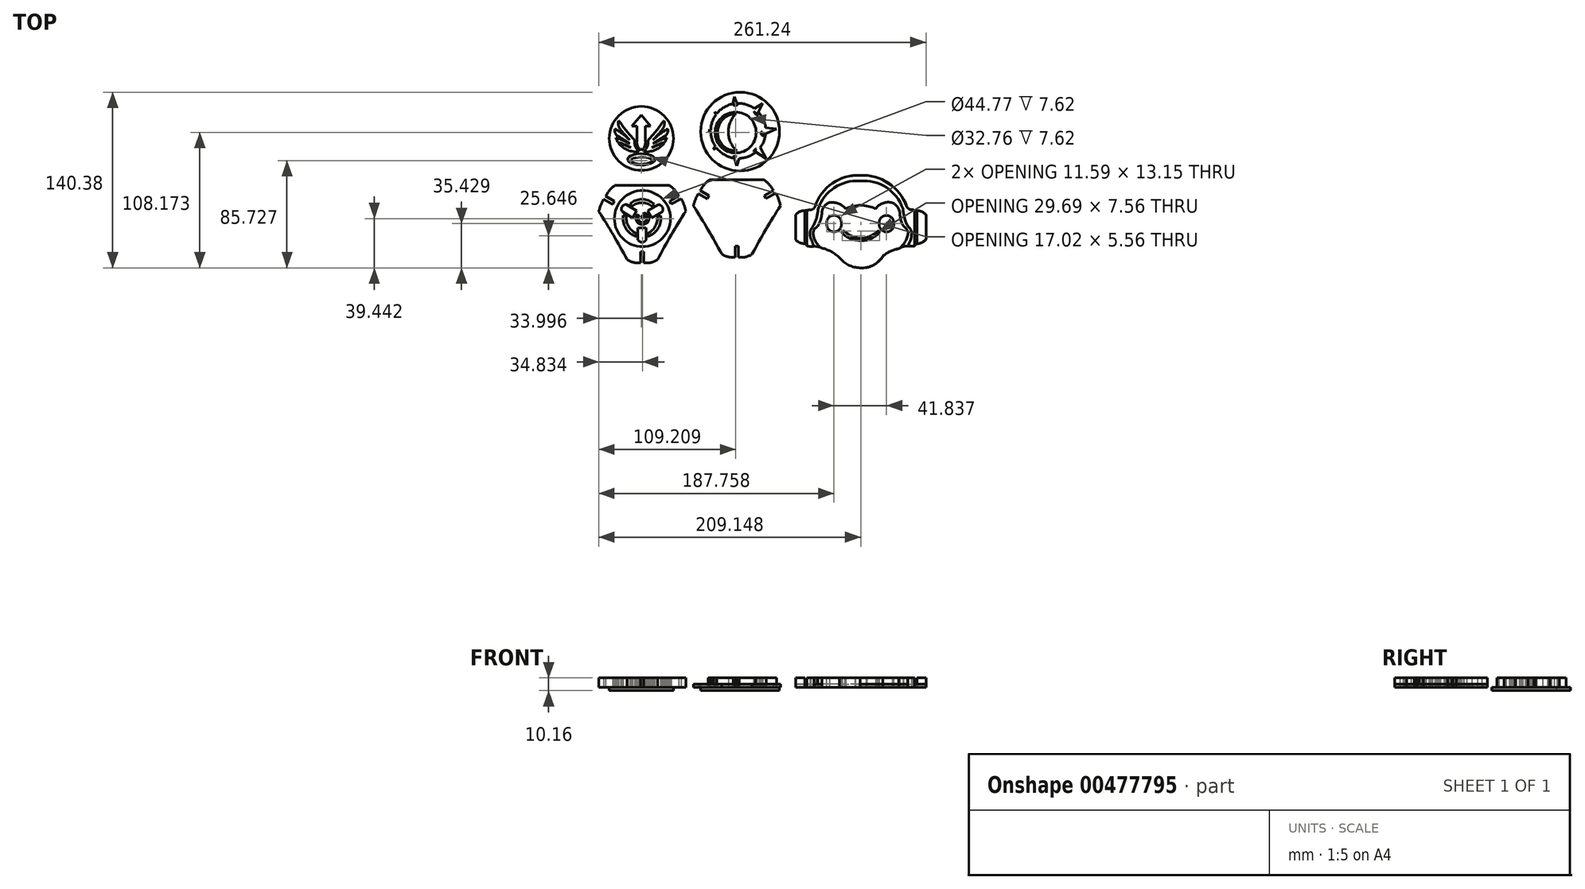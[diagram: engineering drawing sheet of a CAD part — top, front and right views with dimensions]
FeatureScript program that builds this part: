
annotation { "Feature Type Name" : "Feature", "Feature Type Description" : "" }
export const myFeature = defineFeature(function(context is Context, id is Id, definition is map)
    precondition{}
    {
        {
            var Q0;
            Q0=qCreatedBy(makeId("Top.planeOp"),FACE);
            var sketch = newSketch(context, id + "F0", { "sketchPlane" : qUnion([Q0])});
            skEllipse(sketch, "E0", {"center": v(-39.47, 12.8) * mm, "majorRadius": 10.93 * mm, "minorRadius": 4.55 * mm, "majorAxis": v(1, 0)});
            skArc(sketch, "E1", {"start": v(-39.47, 19.86) * mm, "mid": v(-36.84, 23.18) * mm, "end": v(-36.13, 27.35) * mm});
            skArc(sketch, "E2", {"start": v(-43.11, 27.35) * mm, "mid": v(-42.33, 23.1) * mm, "end": v(-39.47, 19.86) * mm});
            skLineSegment(sketch, "E3", {"start": v(-43.11, 27.35) * mm, "end": v(-43.11, 39.24) * mm});
            skLineSegment(sketch, "E4", {"start": v(-43.11, 39.24) * mm, "end": v(-46.93, 39.24) * mm});
            skLineSegment(sketch, "E5", {"start": v(-46.93, 39.24) * mm, "end": v(-39.47, 48.4) * mm});
            skLineSegment(sketch, "E6", {"start": v(-32.01, 39.24) * mm, "end": v(-36.13, 39.24) * mm});
            skLineSegment(sketch, "E7", {"start": v(-36.13, 39.24) * mm, "end": v(-36.13, 27.35) * mm});
            skLineSegment(sketch, "E8", {"start": v(-39.47, 48.4) * mm, "end": v(-32.01, 39.24) * mm});
            skArc(sketch, "E9", {"start": v(-37.54, 18.8) * mm, "mid": v(-34.69, 23.18) * mm, "end": v(-34.02, 28.37) * mm});
            skArc(sketch, "E10", {"start": v(-34.02, 28.37) * mm, "mid": v(-27.34, 35.86) * mm, "end": v(-21.41, 43.96) * mm});
            skArc(sketch, "E11", {"start": v(-22.85, 36.5) * mm, "mid": v(-21.16, 40.04) * mm, "end": v(-21.41, 43.96) * mm});
            skArc(sketch, "E12", {"start": v(-30.14, 28.37) * mm, "mid": v(-26.4, 32.35) * mm, "end": v(-22.85, 36.5) * mm});
            skArc(sketch, "E13", {"start": v(-18.2, 37.18) * mm, "mid": v(-24.47, 33.19) * mm, "end": v(-30.14, 28.37) * mm});
            skArc(sketch, "E14", {"start": v(-20.06, 31.85) * mm, "mid": v(-18.46, 34.28) * mm, "end": v(-18.2, 37.18) * mm});
            skArc(sketch, "E15", {"start": v(-20.06, 31.85) * mm, "mid": v(-25.18, 28.7) * mm, "end": v(-30.14, 25.33) * mm});
            skArc(sketch, "E16", {"start": v(-19.04, 29.98) * mm, "mid": v(-24.75, 28.03) * mm, "end": v(-30.14, 25.33) * mm});
            skArc(sketch, "E17", {"start": v(-20.84, 26.31) * mm, "mid": v(-19.86, 28.1) * mm, "end": v(-19.04, 29.98) * mm});
            skArc(sketch, "E18", {"start": v(-20.84, 26.31) * mm, "mid": v(-26.11, 24.59) * mm, "end": v(-31.06, 22.08) * mm});
            skArc(sketch, "E19", {"start": v(-21.41, 25.33) * mm, "mid": v(-26.37, 24.08) * mm, "end": v(-31.06, 22.08) * mm});
            skArc(sketch, "E20", {"start": v(-37.54, 18.8) * mm, "mid": v(-28.73, 20.22) * mm, "end": v(-21.41, 25.33) * mm});
            skLineSegment(sketch, "E21", {"start": v(-39.47, 59.1) * mm, "end": v(-39.47, -8.7) * mm, "construction": true});
            skArc(sketch, "E22.MirrorCS", {"start": v(-44.92, 28.37) * mm, "mid": v(-51.6, 35.86) * mm, "end": v(-57.52, 43.96) * mm});
            skArc(sketch, "E23.MirrorCS", {"start": v(-56.08, 36.5) * mm, "mid": v(-57.78, 40.04) * mm, "end": v(-57.52, 43.96) * mm});
            skArc(sketch, "E24.MirrorCS", {"start": v(-48.8, 28.37) * mm, "mid": v(-52.54, 32.35) * mm, "end": v(-56.08, 36.5) * mm});
            skArc(sketch, "E25.MirrorCS", {"start": v(-60.74, 37.18) * mm, "mid": v(-54.46, 33.19) * mm, "end": v(-48.8, 28.37) * mm});
            skArc(sketch, "E26.MirrorCS", {"start": v(-58.88, 31.85) * mm, "mid": v(-60.48, 34.28) * mm, "end": v(-60.74, 37.18) * mm});
            skArc(sketch, "E27.MirrorCS", {"start": v(-58.88, 31.85) * mm, "mid": v(-53.76, 28.7) * mm, "end": v(-48.8, 25.33) * mm});
            skArc(sketch, "E28.MirrorCS", {"start": v(-59.9, 29.98) * mm, "mid": v(-54.19, 28.03) * mm, "end": v(-48.8, 25.33) * mm});
            skArc(sketch, "E29.MirrorCS", {"start": v(-58.1, 26.31) * mm, "mid": v(-59.07, 28.1) * mm, "end": v(-59.9, 29.98) * mm});
            skArc(sketch, "E30.MirrorCS", {"start": v(-58.1, 26.31) * mm, "mid": v(-52.82, 24.59) * mm, "end": v(-47.87, 22.08) * mm});
            skArc(sketch, "E31.MirrorCS", {"start": v(-57.52, 25.33) * mm, "mid": v(-52.57, 24.08) * mm, "end": v(-47.87, 22.08) * mm});
            skArc(sketch, "E32.MirrorCS", {"start": v(-41.4, 18.8) * mm, "mid": v(-50.2, 20.22) * mm, "end": v(-57.52, 25.33) * mm});
            skArc(sketch, "E33.MirrorCS", {"start": v(-41.4, 18.8) * mm, "mid": v(-44.25, 23.18) * mm, "end": v(-44.92, 28.37) * mm});
            skSolve(sketch);
        }
        {
            var Q0;
            Q0 = qSketchRegion(id + "F0", true);
            extrude(context, id + "F1", {"entities" : qUnion([Q0]), "depth" : 7.62 * mm, "offsetDistance" : 25.4 * mm});
        }
        {
            var Q0;
            Q0=makeQuery(id+"F1.opExtrude","CAP_FACE",FACE,{"disambiguationData":[OSD([sQuery(id+"F0.wireOp",EDGE,"E0")])],"isStart":false});
            var sketch = newSketch(context, id + "F2", { "sketchPlane" : qUnion([Q0])});
            skEllipse(sketch, "E34", {"center": v(-39.42, 11.8) * mm, "majorRadius": 8.5 * mm, "minorRadius": 2.78 * mm, "majorAxis": v(1, 0)});
            skSolve(sketch);
        }
        {
            var Q0;
            Q0 = qSketchRegion(id + "F2", true);
            extrude(context, id + "F3", {"entities" : qUnion([Q0]), "operationType" : NewBodyOperationType.REMOVE, "oppositeDirection" : true, "depth" : 10.16 * mm, "offsetDistance" : 25.4 * mm});
        }
        {
            var Q0;
            Q0=qCreatedBy(makeId("Top.planeOp"),FACE);
            var sketch = newSketch(context, id + "F4", { "sketchPlane" : qUnion([Q0])});
            skCircle(sketch, "E35", {"center": v(37.9, 35.55) * mm, "radius": 22 * mm});
            skLineSegment(sketch, "E36", {"start": v(33.1, 54.95) * mm, "end": v(34.78, 62.86) * mm});
            skLineSegment(sketch, "E37", {"start": v(34.78, 62.86) * mm, "end": v(37.66, 54.71) * mm});
            skLineSegment(sketch, "E38", {"start": v(37.66, 54.71) * mm, "end": v(33.1, 54.95) * mm});
            skLineSegment(sketch, "E39", {"start": v(47.96, 51.6) * mm, "end": v(57.46, 57.33) * mm});
            skLineSegment(sketch, "E40", {"start": v(57.46, 57.33) * mm, "end": v(52.27, 47.29) * mm});
            skLineSegment(sketch, "E41", {"start": v(52.27, 47.29) * mm, "end": v(47.96, 51.6) * mm});
            skLineSegment(sketch, "E42", {"start": v(56.58, 38.7) * mm, "end": v(68.54, 37) * mm});
            skLineSegment(sketch, "E43", {"start": v(68.54, 37) * mm, "end": v(54.44, 31.15) * mm});
            skLineSegment(sketch, "E44", {"start": v(54.44, 31.15) * mm, "end": v(56.58, 38.7) * mm});
            skLineSegment(sketch, "E45", {"start": v(52.3, 28.3) * mm, "end": v(60.12, 13.3) * mm});
            skLineSegment(sketch, "E46", {"start": v(60.12, 13.3) * mm, "end": v(46.46, 22.46) * mm});
            skLineSegment(sketch, "E47", {"start": v(46.46, 22.46) * mm, "end": v(52.3, 28.3) * mm});
            skLineSegment(sketch, "E48", {"start": v(40.3, 18.87) * mm, "end": v(36.67, 7.48) * mm});
            skLineSegment(sketch, "E49", {"start": v(36.67, 7.48) * mm, "end": v(32.79, 19.35) * mm});
            skLineSegment(sketch, "E50", {"start": v(32.79, 19.35) * mm, "end": v(40.3, 18.87) * mm});
            skLineSegment(sketch, "E51", {"start": v(21.25, 25.6) * mm, "end": v(23.53, 23.32) * mm});
            skLineSegment(sketch, "E52", {"start": v(19.4, 37) * mm, "end": v(18.83, 34) * mm});
            skLineSegment(sketch, "E53", {"start": v(21.25, 46.25) * mm, "end": v(18.83, 50.9) * mm});
            skLineSegment(sketch, "E54", {"start": v(18.83, 50.9) * mm, "end": v(23.53, 47.82) * mm});
            skLineSegment(sketch, "E55", {"start": v(23.53, 47.82) * mm, "end": v(21.25, 46.25) * mm});
            skLineSegment(sketch, "E56", {"start": v(21.25, 25.6) * mm, "end": v(18, 20.57) * mm});
            skLineSegment(sketch, "E57", {"start": v(18, 20.57) * mm, "end": v(23.53, 23.32) * mm});
            skLineSegment(sketch, "E58", {"start": v(18.83, 34) * mm, "end": v(13.83, 35.9) * mm});
            skLineSegment(sketch, "E59", {"start": v(13.83, 35.9) * mm, "end": v(19.4, 37) * mm});
            skSolve(sketch);
        }
        {
            var Q0;
            Q0 = qSketchRegion(id + "F4", true);
            extrude(context, id + "F5", {"entities" : qUnion([Q0]), "depth" : 7.62 * mm, "offsetDistance" : 25.4 * mm});
        }
        {
            var Q0;
            Q0=makeQuery(id+"F5.opExtrude","CAP_FACE",FACE,{"disambiguationData":[OSD([sQuery(id+"F4.wireOp",EDGE,"E35"),sQuery(id+"F4.wireOp",EDGE,"E36"),sQuery(id+"F4.wireOp",EDGE,"E37"),sQuery(id+"F4.wireOp",EDGE,"E39"),sQuery(id+"F4.wireOp",EDGE,"E40"),sQuery(id+"F4.wireOp",EDGE,"E42"),sQuery(id+"F4.wireOp",EDGE,"E43"),sQuery(id+"F4.wireOp",EDGE,"E45"),sQuery(id+"F4.wireOp",EDGE,"E46"),sQuery(id+"F4.wireOp",EDGE,"E48"),sQuery(id+"F4.wireOp",EDGE,"E49"),sQuery(id+"F4.wireOp",EDGE,"lFvAN2aY-k7Z1-D6F1-dTq4-gRtL9pACbP7c"),sQuery(id+"F4.wireOp",EDGE,"jxr9UWhJ-qfHT-bBvY-aeZa-IXjNacF00unG"),sQuery(id+"F4.wireOp",EDGE,"2JyZSbPP-UnY0-dJu7-hiOL-rgGKe5CIZ8wm"),sQuery(id+"F4.wireOp",EDGE,"D89O3qcm-xly6-wlmF-0ntx-pCZKfBFehd9C"),sQuery(id+"F4.wireOp",EDGE,"E53"),sQuery(id+"F4.wireOp",EDGE,"E54")])],"isStart":false});
            var sketch = newSketch(context, id + "F6", { "sketchPlane" : qUnion([Q0])});
            skCircle(sketch, "E60", {"center": v(35.79, 34.25) * mm, "radius": 16.38 * mm});
            skPoint(sketch, "E60.first.point", {"position": v(19.41, 34.57) * mm});
            skPoint(sketch, "E60.second.point", {"position": v(52.17, 34.57) * mm});
            skPoint(sketch, "E60.third.point", {"position": v(42.9, 49) * mm});
            skLineSegment(sketch, "E61", {"start": v(36.67, 57.51) * mm, "end": v(36.93, 56.85) * mm});
            skArc(sketch, "E62", {"start": v(37.26, 57.54) * mm, "mid": v(36.95, 57.93) * mm, "end": v(36.67, 57.51) * mm});
            skArc(sketch, "E63", {"start": v(34.61, 56.5) * mm, "mid": v(35.8, 56.52) * mm, "end": v(36.93, 56.85) * mm});
            skArc(sketch, "E64", {"start": v(34.61, 55.75) * mm, "mid": v(35.78, 55.84) * mm, "end": v(36.9, 56.13) * mm});
            skLineSegment(sketch, "E65", {"start": v(59.79, 33.37) * mm, "end": v(57.57, 32.45) * mm});
            skArc(sketch, "E66", {"start": v(57.06, 34.3) * mm, "mid": v(57.21, 33.34) * mm, "end": v(57.57, 32.45) * mm});
            skLineSegment(sketch, "E67", {"start": v(58.16, 31.82) * mm, "end": v(60.29, 32.7) * mm});
            skLineSegment(sketch, "E68", {"start": v(60.29, 32.7) * mm, "end": v(59.79, 33.37) * mm});
            skLineSegment(sketch, "E69", {"start": v(52.06, 18.71) * mm, "end": v(51.37, 19.17) * mm});
            skArc(sketch, "E70", {"start": v(52.44, 21.37) * mm, "mid": v(51.66, 20.39) * mm, "end": v(51.37, 19.17) * mm});
            skArc(sketch, "E71", {"start": v(52.44, 21.37) * mm, "mid": v(51.12, 20.55) * mm, "end": v(50.39, 19.17) * mm});
            skLineSegment(sketch, "E72", {"start": v(50.39, 19.17) * mm, "end": v(51.93, 18.14) * mm});
            skLineSegment(sketch, "E73", {"start": v(51.93, 18.14) * mm, "end": v(52.06, 18.71) * mm});
            skLineSegment(sketch, "E74", {"start": v(53.97, 50.57) * mm, "end": v(53.28, 49.24) * mm});
            skLineSegment(sketch, "E75", {"start": v(53.86, 48.6) * mm, "end": v(55.03, 50.86) * mm});
            skLineSegment(sketch, "E76", {"start": v(55.03, 50.86) * mm, "end": v(53.97, 50.57) * mm});
            skArc(sketch, "E77", {"start": v(50.65, 51.26) * mm, "mid": v(51.75, 49.97) * mm, "end": v(53.28, 49.24) * mm});
            skArc(sketch, "E78", {"start": v(50.65, 51.26) * mm, "mid": v(51.39, 49.24) * mm, "end": v(53.3, 48.23) * mm});
            skLineSegment(sketch, "E79", {"start": v(34.6, 13.8) * mm, "end": v(34.4, 14.45) * mm});
            skArc(sketch, "E80", {"start": v(36.28, 15) * mm, "mid": v(35.3, 14.88) * mm, "end": v(34.4, 14.45) * mm});
            skArc(sketch, "E81", {"start": v(36.28, 15) * mm, "mid": v(34.94, 15.27) * mm, "end": v(33.66, 14.76) * mm});
            skLineSegment(sketch, "E82", {"start": v(33.66, 14.76) * mm, "end": v(34.12, 13.36) * mm});
            skLineSegment(sketch, "E83", {"start": v(34.12, 13.36) * mm, "end": v(34.6, 13.8) * mm});
            skArc(sketch, "E84", {"start": v(56.77, 34.99) * mm, "mid": v(56.9, 34.63) * mm, "end": v(57.06, 34.3) * mm});
            skArc(sketch, "E85", {"start": v(53.3, 48.23) * mm, "mid": v(53.62, 48.34) * mm, "end": v(53.86, 48.6) * mm});
            skArc(sketch, "E86", {"start": v(56.77, 34.99) * mm, "mid": v(56.3, 34.58) * mm, "end": v(56.13, 33.97) * mm});
            skArc(sketch, "E87", {"start": v(56.13, 33.97) * mm, "mid": v(56.36, 32.83) * mm, "end": v(56.98, 31.85) * mm});
            skArc(sketch, "E88", {"start": v(56.98, 31.85) * mm, "mid": v(57.57, 31.71) * mm, "end": v(58.16, 31.82) * mm});
            skArc(sketch, "E89", {"start": v(34.61, 56.5) * mm, "mid": v(34.33, 56.49) * mm, "end": v(34.09, 56.33) * mm});
            skArc(sketch, "E90", {"start": v(34.09, 56.33) * mm, "mid": v(34.26, 55.96) * mm, "end": v(34.61, 55.75) * mm});
            skArc(sketch, "E91", {"start": v(36.9, 56.13) * mm, "mid": v(37.52, 56.72) * mm, "end": v(37.26, 57.54) * mm});
            skSolve(sketch);
        }
        {
            var Q0;
            Q0 = qSketchRegion(id + "F6", true);
            extrude(context, id + "F7", {"entities" : qUnion([Q0]), "operationType" : NewBodyOperationType.REMOVE, "oppositeDirection" : true, "depth" : 10.16 * mm, "offsetDistance" : 25.4 * mm});
        }
        {
            var Q0;
            Q0=qCreatedBy(makeId("Top.planeOp"),FACE);
            var sketch = newSketch(context, id + "F8", { "sketchPlane" : qUnion([Q0])});
            skArc(sketch, "E92", {"start": v(35.97, 49.24) * mm, "mid": v(21.34, 33.96) * mm, "end": v(36.82, 19.55) * mm});
            skArc(sketch, "E93", {"start": v(35.97, 49.24) * mm, "mid": v(30, 34.2) * mm, "end": v(36.82, 19.55) * mm});
            skSolve(sketch);
        }
        {
            var Q0;
            Q0 = qSketchRegion(id + "F8", true);
            extrude(context, id + "F9", {"entities" : qUnion([Q0]), "depth" : 7.62 * mm, "offsetDistance" : 25.4 * mm});
        }
        {
            var Q0;
            Q0=qCreatedBy(makeId("Top.planeOp"),FACE);
            var sketch = newSketch(context, id + "F10", { "sketchPlane" : qUnion([Q0])});
            skArc(sketch, "E94", {"start": v(-50.93, -67.1) * mm, "mid": v(-61.81, -47.72) * mm, "end": v(-73.42, -28.77) * mm});
            skArc(sketch, "E95", {"start": v(-69.5, -19.18) * mm, "mid": v(-71.85, -23.81) * mm, "end": v(-73.42, -28.77) * mm});
            skLineSegment(sketch, "E96", {"start": v(-69.5, -19.18) * mm, "end": v(-62.35, -23.13) * mm});
            skLineSegment(sketch, "E97", {"start": v(-62.35, -23.13) * mm, "end": v(-61.02, -20.72) * mm});
            skLineSegment(sketch, "E98", {"start": v(-61.02, -20.72) * mm, "end": v(-67.87, -16.43) * mm});
            skArc(sketch, "E99", {"start": v(-60.6, -8.06) * mm, "mid": v(-64.75, -11.8) * mm, "end": v(-67.87, -16.43) * mm});
            skLineSegment(sketch, "E100", {"start": v(-60.6, -8.06) * mm, "end": v(-16.9, -8.06) * mm});
            skArc(sketch, "E101", {"start": v(-9.62, -16.43) * mm, "mid": v(-12.8, -11.84) * mm, "end": v(-16.9, -8.06) * mm});
            skLineSegment(sketch, "E102", {"start": v(-9.62, -16.43) * mm, "end": v(-16.88, -20.7) * mm});
            skLineSegment(sketch, "E103", {"start": v(-16.88, -20.7) * mm, "end": v(-15.53, -23) * mm});
            skLineSegment(sketch, "E104", {"start": v(-15.53, -23) * mm, "end": v(-7.67, -18.62) * mm});
            skArc(sketch, "E105", {"start": v(-3.93, -28.59) * mm, "mid": v(-5.43, -23.47) * mm, "end": v(-7.67, -18.62) * mm});
            skArc(sketch, "E106", {"start": v(-3.93, -28.59) * mm, "mid": v(-15.66, -47.74) * mm, "end": v(-26.59, -67.38) * mm});
            skArc(sketch, "E107", {"start": v(-50.93, -67.1) * mm, "mid": v(-45.82, -69.52) * mm, "end": v(-40.18, -69.82) * mm});
            skLineSegment(sketch, "E108", {"start": v(-40.18, -69.82) * mm, "end": v(-40.18, -60.92) * mm});
            skLineSegment(sketch, "E109", {"start": v(-40.18, -60.92) * mm, "end": v(-37.45, -60.92) * mm});
            skLineSegment(sketch, "E110", {"start": v(-37.45, -60.92) * mm, "end": v(-37.45, -69.82) * mm});
            skArc(sketch, "E111", {"start": v(-37.45, -69.82) * mm, "mid": v(-31.8, -69.59) * mm, "end": v(-26.59, -67.38) * mm});
            skSolve(sketch);
        }
        {
            var Q0;
            Q0 = qSketchRegion(id + "F10", true);
            extrude(context, id + "F11", {"entities" : qUnion([Q0]), "depth" : 7.62 * mm, "offsetDistance" : 25.4 * mm});
        }
        {
            var Q0;
            Q0=makeQuery(id+"F11.opExtrude","CAP_FACE",FACE,{"disambiguationData":[OSD([sQuery(id+"F10.wireOp",EDGE,"E94"),sQuery(id+"F10.wireOp",EDGE,"E95"),sQuery(id+"F10.wireOp",EDGE,"E96"),sQuery(id+"F10.wireOp",EDGE,"E97"),sQuery(id+"F10.wireOp",EDGE,"E98"),sQuery(id+"F10.wireOp",EDGE,"E99"),sQuery(id+"F10.wireOp",EDGE,"E100"),sQuery(id+"F10.wireOp",EDGE,"E101"),sQuery(id+"F10.wireOp",EDGE,"E102"),sQuery(id+"F10.wireOp",EDGE,"E103"),sQuery(id+"F10.wireOp",EDGE,"E104"),sQuery(id+"F10.wireOp",EDGE,"E105"),sQuery(id+"F10.wireOp",EDGE,"E106"),sQuery(id+"F10.wireOp",EDGE,"E107"),sQuery(id+"F10.wireOp",EDGE,"E108"),sQuery(id+"F10.wireOp",EDGE,"E109"),sQuery(id+"F10.wireOp",EDGE,"E110"),sQuery(id+"F10.wireOp",EDGE,"E111")])],"isStart":false});
            var sketch = newSketch(context, id + "F12", { "sketchPlane" : qUnion([Q0])});
            skCircle(sketch, "E112", {"center": v(-38.59, -34.48) * mm, "radius": 22.38 * mm});
            skSolve(sketch);
        }
        {
            var Q0;
            Q0 = qSketchRegion(id + "F12", true);
            extrude(context, id + "F13", {"entities" : qUnion([Q0]), "operationType" : NewBodyOperationType.REMOVE, "oppositeDirection" : true, "depth" : 25.4 * mm, "offsetDistance" : 25.4 * mm});
        }
        {
            var Q0;
            Q0=qCreatedBy(makeId("Top.planeOp"),FACE);
            var sketch = newSketch(context, id + "F14", { "sketchPlane" : qUnion([Q0])});
            skLineSegment(sketch, "E113", {"start": v(-42.22, -41.82) * mm, "end": v(-35.6, -41.82) * mm});
            skLineSegment(sketch, "E114", {"start": v(-35.6, -41.82) * mm, "end": v(-35.6, -51.3) * mm});
            skLineSegment(sketch, "E115", {"start": v(-42.22, -41.82) * mm, "end": v(-42.22, -51.3) * mm});
            skArc(sketch, "E116", {"start": v(-42.22, -51.3) * mm, "mid": v(-38.9, -53.4) * mm, "end": v(-35.6, -51.3) * mm});
            skLineSegment(sketch, "E117", {"start": v(-43.22, -28.1) * mm, "end": v(-46.56, -33.83) * mm});
            skLineSegment(sketch, "E118", {"start": v(-46.56, -33.83) * mm, "end": v(-54.74, -29.04) * mm});
            skLineSegment(sketch, "E119", {"start": v(-43.22, -28.1) * mm, "end": v(-51.4, -23.32) * mm});
            skArc(sketch, "E120", {"start": v(-51.4, -23.32) * mm, "mid": v(-54.88, -25.12) * mm, "end": v(-54.74, -29.04) * mm});
            skLineSegment(sketch, "E121.0", {"start": v(-51.4, -23.32) * mm, "end": v(-54.74, -29.04) * mm, "construction": true});
            skLineSegment(sketch, "E122", {"start": v(-31.08, -33.87) * mm, "end": v(-34.39, -28.13) * mm});
            skLineSegment(sketch, "E123", {"start": v(-34.39, -28.13) * mm, "end": v(-26.18, -23.39) * mm});
            skLineSegment(sketch, "E124", {"start": v(-31.08, -33.87) * mm, "end": v(-22.87, -29.13) * mm});
            skArc(sketch, "E125", {"start": v(-22.87, -29.13) * mm, "mid": v(-22.7, -25.21) * mm, "end": v(-26.18, -23.39) * mm});
            skLineSegment(sketch, "E126.0", {"start": v(-22.87, -29.13) * mm, "end": v(-26.18, -23.39) * mm, "construction": true});
            skArc(sketch, "E127", {"start": v(-51.55, -31.93) * mm, "mid": v(-49.83, -40.42) * mm, "end": v(-43.59, -46.41) * mm});
            skLineSegment(sketch, "E128", {"start": v(-51.55, -31.93) * mm, "end": v(-53.95, -31.93) * mm});
            skLineSegment(sketch, "E129", {"start": v(-43.59, -46.41) * mm, "end": v(-43.65, -48.86) * mm});
            skArc(sketch, "E130", {"start": v(-53.95, -31.93) * mm, "mid": v(-51.9, -42.28) * mm, "end": v(-43.65, -48.86) * mm});
            skArc(sketch, "E131.MirrorCS", {"start": v(-26.48, -31.94) * mm, "mid": v(-28.2, -40.42) * mm, "end": v(-34.45, -46.42) * mm});
            skArc(sketch, "E132.MirrorCS", {"start": v(-24.09, -31.94) * mm, "mid": v(-26.14, -42.29) * mm, "end": v(-34.39, -48.86) * mm});
            skLineSegment(sketch, "E133.MirrorCS", {"start": v(-26.48, -31.94) * mm, "end": v(-24.09, -31.94) * mm});
            skLineSegment(sketch, "E134.MirrorCS", {"start": v(-34.45, -46.42) * mm, "end": v(-34.39, -48.86) * mm});
            skLineSegment(sketch, "E135", {"start": v(-46.94, -24.7) * mm, "end": v(-48.37, -22.61) * mm});
            skLineSegment(sketch, "E136", {"start": v(-31.02, -24.7) * mm, "end": v(-29.4, -22.76) * mm});
            skArc(sketch, "E137", {"start": v(-29.4, -22.76) * mm, "mid": v(-38.85, -19.13) * mm, "end": v(-48.37, -22.61) * mm});
            skArc(sketch, "E138", {"start": v(-31.02, -24.7) * mm, "mid": v(-38.98, -21.9) * mm, "end": v(-46.94, -24.7) * mm});
            skLineSegment(sketch, "E139", {"start": v(-42.47, -31.32) * mm, "end": v(-41.2, -32.2) * mm});
            skArc(sketch, "E140", {"start": v(-41.2, -32.2) * mm, "mid": v(-41.75, -35.3) * mm, "end": v(-39.36, -37.38) * mm});
            skArc(sketch, "E141", {"start": v(-39.36, -37.38) * mm, "mid": v(-36.44, -36.71) * mm, "end": v(-35.3, -33.95) * mm});
            skArc(sketch, "E142", {"start": v(-35.3, -33.95) * mm, "mid": v(-35.66, -32.87) * mm, "end": v(-36.6, -32.2) * mm});
            skLineSegment(sketch, "E143", {"start": v(-36.6, -32.2) * mm, "end": v(-38.37, -34.65) * mm});
            skLineSegment(sketch, "E144", {"start": v(-38.37, -34.65) * mm, "end": v(-39.73, -33.66) * mm});
            skLineSegment(sketch, "E145", {"start": v(-39.73, -33.66) * mm, "end": v(-37.07, -30) * mm});
            skArc(sketch, "E146", {"start": v(-34.84, -37.9) * mm, "mid": v(-33.51, -33.26) * mm, "end": v(-37.07, -30) * mm});
            skArc(sketch, "E147", {"start": v(-42.47, -31.32) * mm, "mid": v(-43.65, -35.6) * mm, "end": v(-40.67, -38.88) * mm});
            skArc(sketch, "E148", {"start": v(-40.67, -38.88) * mm, "mid": v(-37.62, -39.2) * mm, "end": v(-34.84, -37.9) * mm});
            skSolve(sketch);
        }
        {
            var Q0;
            Q0 = qSketchRegion(id + "F14", true);
            extrude(context, id + "F15", {"entities" : qUnion([Q0]), "depth" : 7.62 * mm, "offsetDistance" : 25.4 * mm});
        }
        {
            var Q0;
            Q0=qCreatedBy(makeId("Top.planeOp"),FACE);
            var sketch = newSketch(context, id + "F16", { "sketchPlane" : qUnion([Q0])});
            skArc(sketch, "E149", {"start": v(24.6, -62.68) * mm, "mid": v(13.72, -43.3) * mm, "end": v(2.11, -24.34) * mm});
            skArc(sketch, "E150", {"start": v(6.03, -14.76) * mm, "mid": v(3.68, -19.4) * mm, "end": v(2.11, -24.34) * mm});
            skLineSegment(sketch, "E151", {"start": v(6.03, -14.76) * mm, "end": v(13.19, -18.7) * mm});
            skLineSegment(sketch, "E152", {"start": v(13.19, -18.7) * mm, "end": v(14.51, -16.3) * mm});
            skLineSegment(sketch, "E153", {"start": v(14.51, -16.3) * mm, "end": v(7.66, -12) * mm});
            skArc(sketch, "E154", {"start": v(14.94, -3.64) * mm, "mid": v(10.78, -7.37) * mm, "end": v(7.66, -12) * mm});
            skLineSegment(sketch, "E155", {"start": v(14.94, -3.64) * mm, "end": v(58.63, -3.64) * mm});
            skArc(sketch, "E156", {"start": v(65.91, -12) * mm, "mid": v(62.73, -7.42) * mm, "end": v(58.63, -3.64) * mm});
            skLineSegment(sketch, "E157", {"start": v(65.91, -12) * mm, "end": v(58.65, -16.29) * mm});
            skLineSegment(sketch, "E158", {"start": v(58.65, -16.29) * mm, "end": v(60, -18.58) * mm});
            skLineSegment(sketch, "E159", {"start": v(60, -18.58) * mm, "end": v(67.87, -14.2) * mm});
            skArc(sketch, "E160", {"start": v(71.6, -24.16) * mm, "mid": v(70.1, -19.04) * mm, "end": v(67.87, -14.2) * mm});
            skArc(sketch, "E161", {"start": v(71.6, -24.16) * mm, "mid": v(59.87, -43.32) * mm, "end": v(48.94, -62.95) * mm});
            skArc(sketch, "E162", {"start": v(24.6, -62.68) * mm, "mid": v(29.71, -65.1) * mm, "end": v(35.35, -65.4) * mm});
            skLineSegment(sketch, "E163", {"start": v(35.35, -65.4) * mm, "end": v(35.35, -56.5) * mm});
            skLineSegment(sketch, "E164", {"start": v(35.35, -56.5) * mm, "end": v(38.09, -56.5) * mm});
            skLineSegment(sketch, "E165", {"start": v(38.09, -56.5) * mm, "end": v(38.09, -65.4) * mm});
            skArc(sketch, "E166", {"start": v(38.09, -65.4) * mm, "mid": v(43.74, -65.16) * mm, "end": v(48.94, -62.95) * mm});
            skSolve(sketch);
        }
        {
            var Q0;
            Q0 = qSketchRegion(id + "F16", true);
            extrude(context, id + "F17", {"entities" : qUnion([Q0]), "depth" : 2.54 * mm, "offsetDistance" : 25.4 * mm});
        }
        {
            var Q0;
            Q0=qCreatedBy(makeId("Top.planeOp"),FACE);
            var sketch = newSketch(context, id + "F18", { "sketchPlane" : qUnion([Q0])});
            skArc(sketch, "E167", {"start": v(135.1, -73.85) * mm, "mid": v(145.56, -71.78) * mm, "end": v(153.35, -64.48) * mm});
            skArc(sketch, "E168", {"start": v(166.01, -58.55) * mm, "mid": v(159.28, -60.66) * mm, "end": v(153.35, -64.48) * mm});
            skArc(sketch, "E169", {"start": v(166.01, -58.55) * mm, "mid": v(171.09, -53) * mm, "end": v(173.58, -45.9) * mm});
            skArc(sketch, "E170", {"start": v(173.58, -45.9) * mm, "mid": v(172.2, -42.79) * mm, "end": v(169.82, -40.38) * mm});
            skArc(sketch, "E171", {"start": v(167.05, -31.44) * mm, "mid": v(167.77, -36.12) * mm, "end": v(169.82, -40.38) * mm});
            skArc(sketch, "E172", {"start": v(167.05, -31.44) * mm, "mid": v(165.37, -25.8) * mm, "end": v(161.03, -21.83) * mm});
            skArc(sketch, "E173", {"start": v(161.03, -21.83) * mm, "mid": v(153.52, -22.16) * mm, "end": v(147.55, -26.74) * mm});
            skArc(sketch, "E174", {"start": v(147.55, -26.74) * mm, "mid": v(135.64, -23.92) * mm, "end": v(123.73, -26.74) * mm});
            skArc(sketch, "E175", {"start": v(123.73, -26.74) * mm, "mid": v(117.89, -22.59) * mm, "end": v(110.78, -21.6) * mm});
            skArc(sketch, "E176", {"start": v(110.78, -21.6) * mm, "mid": v(106.15, -25.28) * mm, "end": v(104.62, -31) * mm});
            skArc(sketch, "E177", {"start": v(101.2, -40.87) * mm, "mid": v(103.37, -36.1) * mm, "end": v(104.62, -31) * mm});
            skArc(sketch, "E178", {"start": v(101.2, -40.87) * mm, "mid": v(99.22, -42.45) * mm, "end": v(97.87, -44.59) * mm});
            skArc(sketch, "E179", {"start": v(97.87, -44.59) * mm, "mid": v(98.4, -50.18) * mm, "end": v(101.2, -55.05) * mm});
            skArc(sketch, "E180", {"start": v(101.2, -55.05) * mm, "mid": v(102.77, -56.7) * mm, "end": v(104.62, -58.02) * mm});
            skArc(sketch, "E181", {"start": v(118.77, -65.67) * mm, "mid": v(112.2, -60.93) * mm, "end": v(104.62, -58.02) * mm});
            skArc(sketch, "E182", {"start": v(118.77, -65.67) * mm, "mid": v(126, -71.62) * mm, "end": v(135.1, -73.85) * mm});
            skArc(sketch, "E183", {"start": v(95.62, -49.66) * mm, "mid": v(96.95, -53.19) * mm, "end": v(98.46, -56.64) * mm});
            skArc(sketch, "E184", {"start": v(95.62, -43.85) * mm, "mid": v(95.13, -46.76) * mm, "end": v(95.62, -49.66) * mm});
            skArc(sketch, "E185", {"start": v(98.43, -39.3) * mm, "mid": v(96.97, -41.54) * mm, "end": v(95.62, -43.85) * mm});
            skArc(sketch, "E186", {"start": v(98.43, -39.3) * mm, "mid": v(100.65, -33.03) * mm, "end": v(101.74, -26.46) * mm});
            skArc(sketch, "E187", {"start": v(135.1, -4.55) * mm, "mid": v(114.66, -9.78) * mm, "end": v(101.74, -26.46) * mm});
            skArc(sketch, "E188", {"start": v(169.34, -26.74) * mm, "mid": v(156.1, -9.66) * mm, "end": v(135.1, -4.55) * mm});
            skArc(sketch, "E189", {"start": v(169.34, -26.74) * mm, "mid": v(170.64, -33.87) * mm, "end": v(173.19, -40.67) * mm});
            skArc(sketch, "E190", {"start": v(176.27, -44.9) * mm, "mid": v(175.03, -42.56) * mm, "end": v(173.19, -40.67) * mm});
            skArc(sketch, "E191", {"start": v(173.19, -56.4) * mm, "mid": v(175.67, -50.9) * mm, "end": v(176.27, -44.9) * mm});
            skArc(sketch, "E192", {"start": v(173.19, -56.4) * mm, "mid": v(175.92, -56.6) * mm, "end": v(178.65, -56.4) * mm});
            skLineSegment(sketch, "E193", {"start": v(178.65, -56.4) * mm, "end": v(178.65, -29.25) * mm});
            skArc(sketch, "E194", {"start": v(178.65, -29.25) * mm, "mid": v(178.18, -28.05) * mm, "end": v(177.02, -27.5) * mm});
            skArc(sketch, "E195", {"start": v(172.3, -24.82) * mm, "mid": v(174.25, -26.88) * mm, "end": v(177.02, -27.5) * mm});
            skArc(sketch, "E196", {"start": v(172.3, -24.82) * mm, "mid": v(157.83, -6.2) * mm, "end": v(135.1, 0) * mm});
            skArc(sketch, "E197", {"start": v(135.1, 0) * mm, "mid": v(112.92, -6.33) * mm, "end": v(99.14, -24.82) * mm});
            skArc(sketch, "E198", {"start": v(95.77, -27.53) * mm, "mid": v(97.88, -26.7) * mm, "end": v(99.14, -24.82) * mm});
            skArc(sketch, "E199", {"start": v(95.77, -27.53) * mm, "mid": v(93.98, -27.74) * mm, "end": v(92.73, -29.04) * mm});
            skLineSegment(sketch, "E200", {"start": v(92.73, -29.04) * mm, "end": v(92.73, -56.32) * mm});
            skArc(sketch, "E201", {"start": v(92.73, -56.32) * mm, "mid": v(95.58, -56.82) * mm, "end": v(98.46, -56.64) * mm});
            skLineSegment(sketch, "E202", {"start": v(90.96, -54.53) * mm, "end": v(90.96, -28.14) * mm});
            skArc(sketch, "E203", {"start": v(90.96, -28.14) * mm, "mid": v(86.87, -28.96) * mm, "end": v(83.6, -31.56) * mm});
            skLineSegment(sketch, "E204", {"start": v(83.6, -31.56) * mm, "end": v(83.6, -51.38) * mm});
            skArc(sketch, "E205", {"start": v(83.6, -51.38) * mm, "mid": v(86.95, -53.7) * mm, "end": v(90.96, -54.53) * mm});
            skLineSegment(sketch, "E206", {"start": v(180.43, -54.67) * mm, "end": v(180.43, -28.21) * mm});
            skArc(sketch, "E207", {"start": v(187.76, -31.67) * mm, "mid": v(184.53, -29.03) * mm, "end": v(180.43, -28.21) * mm});
            skLineSegment(sketch, "E208", {"start": v(187.76, -31.67) * mm, "end": v(187.76, -51.1) * mm});
            skArc(sketch, "E209", {"start": v(180.43, -54.67) * mm, "mid": v(184.46, -53.63) * mm, "end": v(187.76, -51.1) * mm});
            skSolve(sketch);
        }
        {
            var Q0;
            Q0 = qSketchRegion(id + "F18", true);
            extrude(context, id + "F19", {"entities" : qUnion([Q0]), "depth" : 7.62 * mm, "offsetDistance" : 25.4 * mm});
        }
        {
            var Q0;
            Q0=makeQuery(id+"F19.opExtrude","CAP_FACE",FACE,{"disambiguationData":[OSD([sQuery(id+"F18.wireOp",EDGE,"E167"),sQuery(id+"F18.wireOp",EDGE,"E168"),sQuery(id+"F18.wireOp",EDGE,"E169"),sQuery(id+"F18.wireOp",EDGE,"E170"),sQuery(id+"F18.wireOp",EDGE,"E171"),sQuery(id+"F18.wireOp",EDGE,"E172"),sQuery(id+"F18.wireOp",EDGE,"E173"),sQuery(id+"F18.wireOp",EDGE,"E174"),sQuery(id+"F18.wireOp",EDGE,"E175"),sQuery(id+"F18.wireOp",EDGE,"E176"),sQuery(id+"F18.wireOp",EDGE,"E177"),sQuery(id+"F18.wireOp",EDGE,"E178"),sQuery(id+"F18.wireOp",EDGE,"E179"),sQuery(id+"F18.wireOp",EDGE,"E180"),sQuery(id+"F18.wireOp",EDGE,"E181"),sQuery(id+"F18.wireOp",EDGE,"E182")])],"isStart":false});
            var sketch = newSketch(context, id + "F20", { "sketchPlane" : qUnion([Q0])});
            skArc(sketch, "E210", {"start": v(108.54, -38.47) * mm, "mid": v(114.57, -45.07) * mm, "end": v(120.14, -38.08) * mm});
            skArc(sketch, "E211", {"start": v(120.14, -38.08) * mm, "mid": v(114.12, -31.92) * mm, "end": v(108.54, -38.47) * mm});
            skArc(sketch, "E212", {"start": v(150.38, -38.54) * mm, "mid": v(156.4, -45.13) * mm, "end": v(161.97, -38.15) * mm});
            skArc(sketch, "E213", {"start": v(161.97, -38.15) * mm, "mid": v(155.96, -31.98) * mm, "end": v(150.38, -38.54) * mm});
            skArc(sketch, "E214", {"start": v(123.01, -44.9) * mm, "mid": v(127.14, -47.82) * mm, "end": v(131.8, -49.78) * mm});
            skArc(sketch, "E215", {"start": v(123.01, -44.9) * mm, "mid": v(121.29, -44.8) * mm, "end": v(121.2, -46.53) * mm});
            skArc(sketch, "E216", {"start": v(121.2, -46.53) * mm, "mid": v(125.92, -49.8) * mm, "end": v(131.38, -51.6) * mm});
            skArc(sketch, "E217", {"start": v(140.77, -51.6) * mm, "mid": v(145.98, -49.38) * mm, "end": v(150.47, -45.92) * mm});
            skArc(sketch, "E218", {"start": v(150.47, -45.92) * mm, "mid": v(150.26, -44.75) * mm, "end": v(149.08, -44.72) * mm});
            skArc(sketch, "E219", {"start": v(140.1, -49.74) * mm, "mid": v(144.86, -47.72) * mm, "end": v(149.08, -44.72) * mm});
            skArc(sketch, "E220", {"start": v(131.8, -49.78) * mm, "mid": v(135.95, -50.21) * mm, "end": v(140.1, -49.74) * mm});
            skArc(sketch, "E221", {"start": v(131.38, -51.6) * mm, "mid": v(136.08, -52.06) * mm, "end": v(140.77, -51.6) * mm});
            skSolve(sketch);
        }
        {
            var Q0;
            Q0 = qSketchRegion(id + "F20", true);
            extrude(context, id + "F21", {"entities" : qUnion([Q0]), "operationType" : NewBodyOperationType.REMOVE, "oppositeDirection" : true, "depth" : 25.4 * mm, "offsetDistance" : 25.4 * mm});
        }
        {
            var Q0;
            Q0=qCreatedBy(makeId("Top.planeOp"),FACE);
            var sketch = newSketch(context, id + "F22", { "sketchPlane" : qUnion([Q0])});
            skArc(sketch, "E222", {"start": v(135.15, -73.84) * mm, "mid": v(145.62, -71.77) * mm, "end": v(153.4, -64.47) * mm});
            skArc(sketch, "E223", {"start": v(166.07, -58.55) * mm, "mid": v(159.34, -60.65) * mm, "end": v(153.4, -64.47) * mm});
            skArc(sketch, "E224", {"start": v(118.83, -65.66) * mm, "mid": v(112.25, -60.92) * mm, "end": v(104.68, -58.01) * mm});
            skArc(sketch, "E225", {"start": v(118.83, -65.66) * mm, "mid": v(126.06, -71.61) * mm, "end": v(135.15, -73.84) * mm});
            skArc(sketch, "E226", {"start": v(173.24, -56.39) * mm, "mid": v(175.97, -56.59) * mm, "end": v(178.7, -56.39) * mm});
            skArc(sketch, "E227", {"start": v(172.35, -24.8) * mm, "mid": v(174.34, -26.82) * mm, "end": v(177.1, -27.38) * mm});
            skArc(sketch, "E228", {"start": v(172.35, -24.8) * mm, "mid": v(157.89, -6.2) * mm, "end": v(135.15, 0) * mm});
            skArc(sketch, "E229", {"start": v(135.15, 0) * mm, "mid": v(112.98, -6.32) * mm, "end": v(99.2, -24.8) * mm});
            skArc(sketch, "E230", {"start": v(95.83, -27.52) * mm, "mid": v(97.94, -26.7) * mm, "end": v(99.2, -24.8) * mm});
            skArc(sketch, "E231", {"start": v(92.79, -56.3) * mm, "mid": v(95.63, -56.8) * mm, "end": v(98.51, -56.63) * mm});
            skArc(sketch, "E232", {"start": v(91.02, -28.13) * mm, "mid": v(86.92, -28.95) * mm, "end": v(83.65, -31.55) * mm});
            skLineSegment(sketch, "E233", {"start": v(83.65, -31.55) * mm, "end": v(83.65, -51.37) * mm});
            skArc(sketch, "E234", {"start": v(83.65, -51.37) * mm, "mid": v(87.01, -53.7) * mm, "end": v(91.02, -54.52) * mm});
            skArc(sketch, "E235", {"start": v(187.82, -31.66) * mm, "mid": v(184.58, -29.02) * mm, "end": v(180.49, -28.2) * mm});
            skLineSegment(sketch, "E236", {"start": v(187.82, -31.66) * mm, "end": v(187.82, -51.09) * mm});
            skArc(sketch, "E237", {"start": v(180.49, -54.66) * mm, "mid": v(184.52, -53.62) * mm, "end": v(187.82, -51.09) * mm});
            skArc(sketch, "E238", {"start": v(104.68, -58.01) * mm, "mid": v(101.66, -57.06) * mm, "end": v(98.51, -56.63) * mm});
            skArc(sketch, "E239", {"start": v(92.79, -56.3) * mm, "mid": v(91.93, -55.38) * mm, "end": v(91.02, -54.52) * mm});
            skArc(sketch, "E240", {"start": v(180.49, -54.66) * mm, "mid": v(179.54, -55.47) * mm, "end": v(178.7, -56.39) * mm});
            skArc(sketch, "E241", {"start": v(95.83, -27.52) * mm, "mid": v(93.42, -27.78) * mm, "end": v(91.02, -28.13) * mm});
            skArc(sketch, "E242", {"start": v(173.24, -56.39) * mm, "mid": v(169.52, -57) * mm, "end": v(166.07, -58.55) * mm});
            skArc(sketch, "E243", {"start": v(177.1, -27.38) * mm, "mid": v(178.77, -27.91) * mm, "end": v(180.49, -28.2) * mm});
            skSolve(sketch);
        }
        {
            var Q0;
            Q0 = qSketchRegion(id + "F22", true);
            extrude(context, id + "F23", {"entities" : qUnion([Q0]), "depth" : 2.54 * mm, "offsetDistance" : 25.4 * mm});
        }
        {
            var Q0;
            Q0=qCreatedBy(makeId("Top.planeOp"),FACE);
            var sketch = newSketch(context, id + "F24", { "sketchPlane" : qUnion([Q0])});
            skCircle(sketch, "E244", {"center": v(-39.47, 29.58) * mm, "radius": 25.6 * mm});
            skCircle(sketch, "E245", {"center": v(39.41, 35) * mm, "radius": 31.45 * mm});
            skSolve(sketch);
        }
        {
            var Q0;
            Q0 = qSketchRegion(id + "F24", true);
            extrude(context, id + "F25", {"entities" : qUnion([Q0]), "oppositeDirection" : true, "depth" : 2.54 * mm, "offsetDistance" : 25.4 * mm});
        }
    });
